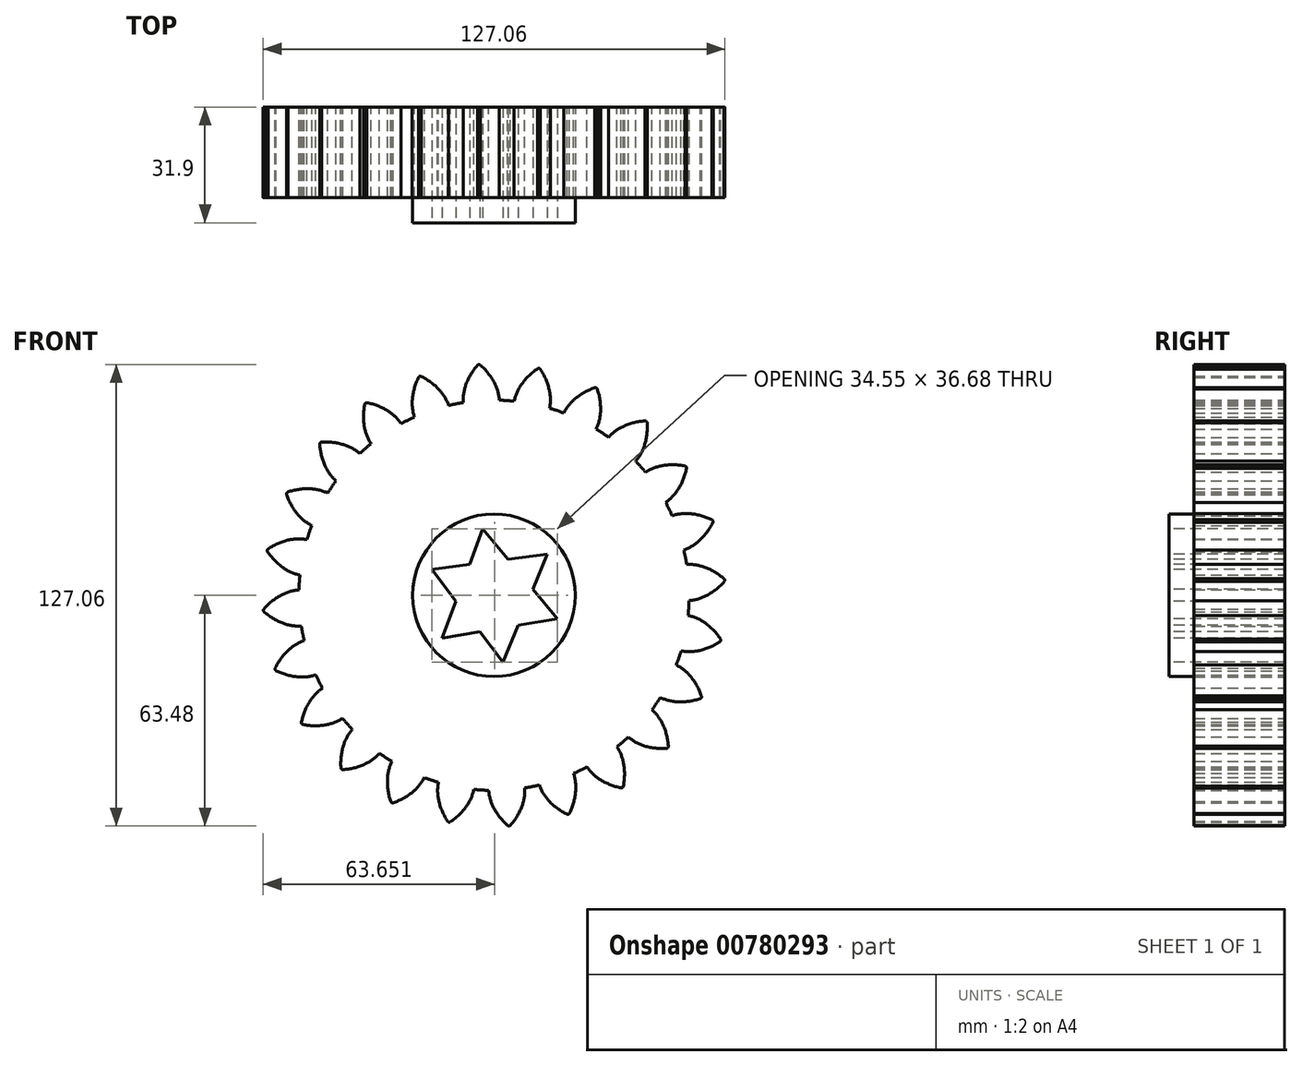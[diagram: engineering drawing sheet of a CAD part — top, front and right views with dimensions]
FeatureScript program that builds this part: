
annotation { "Feature Type Name" : "Feature", "Feature Type Description" : "" }
export const myFeature = defineFeature(function(context is Context, id is Id, definition is map)
    precondition{}
    {
        {
            var Q0;
            Q0=qCreatedBy(makeId("Front.planeOp"),FACE);
            var sketch = newSketch(context, id + "F0", { "sketchPlane" : qUnion([Q0])});
            skCircle(sketch, "E0", {"center": v(0, 0) * mm, "radius": 63.5 * mm, "construction": true});
            skCircle(sketch, "E1", {"center": v(0, 0) * mm, "radius": 53.72 * mm});
            skCircle(sketch, "E2", {"center": v(0, 0) * mm, "radius": 58.67 * mm, "construction": true});
            skLineSegment(sketch, "E3", {"start": v(0, 0) * mm, "end": v(0, 67.7) * mm, "construction": true});
            skLineSegment(sketch, "E4", {"start": v(0, 0) * mm, "end": v(-4.77, 72.78) * mm, "construction": true});
            skLineSegment(sketch, "E5", {"start": v(0, 58.67) * mm, "end": v(-82.08, 58.67) * mm, "construction": true});
            skLineSegment(sketch, "E6", {"start": v(0, 58.67) * mm, "end": v(-77.26, 24.74) * mm, "construction": true});
            skCircle(sketch, "E7", {"center": v(0, 58.67) * mm, "radius": 14.6 * mm, "construction": true});
            skCircle(sketch, "E8", {"center": v(0, 0) * mm, "radius": 53.72 * mm, "construction": true});
            skCircle(sketch, "E9", {"center": v(-13.05, 52.11) * mm, "radius": 14.6 * mm, "construction": true});
            skArc(sketch, "E10", {"start": v(0, 58.67) * mm, "mid": v(-1.67, 61.2) * mm, "end": v(-3.77, 63.39) * mm});
            skArc(sketch, "E11", {"start": v(1.47, 53.7) * mm, "mid": v(1, 56.26) * mm, "end": v(0, 58.67) * mm});
            skArc(sketch, "E12.MirrorCS", {"start": v(-7.66, 58.17) * mm, "mid": v(-6.33, 60.9) * mm, "end": v(-4.54, 63.34) * mm});
            skArc(sketch, "E13", {"start": v(-3.77, 63.39) * mm, "mid": v(-4.16, 63.53) * mm, "end": v(-4.54, 63.34) * mm});
            skArc(sketch, "E14.MirrorCS", {"start": v(-8.47, 53.05) * mm, "mid": v(-8.33, 55.65) * mm, "end": v(-7.66, 58.17) * mm});
            skSolve(sketch);
        }
        {
            var Q0;
            Q0 = qSketchRegion(id + "F0", true);
            extrude(context, id + "F1", {"entities" : qUnion([Q0]), "depth" : 25 * mm, "offsetDistance" : 25 * mm});
        }
        {
            var Q0;
            Q0=makeQuery(id+"F1.opExtrude","SWEPT_BODY",BODY,{"disambiguationData":[OSD([sQuery(id+"F0.wireOp",EDGE,"E1"),sQuery(id+"F0.wireOp",EDGE,"E10"),sQuery(id+"F0.wireOp",EDGE,"E11"),sQuery(id+"F0.wireOp",EDGE,"E12.MirrorCS"),sQuery(id+"F0.wireOp",EDGE,"E13"),sQuery(id+"F0.wireOp",EDGE,"E14.MirrorCS")])]});
            var Q1;
            Q1=makeQuery(id+"F1.opExtrude","SWEPT_FACE",FACE,{"disambiguationData":[OSD([sQuery(id+"F0.wireOp",EDGE,"E1")])]});
            circularPattern(context, id + "F2", {"operationType" : NewBodyOperationType.ADD, "entities" : qUnion([Q0]), "axis" : qUnion([Q1]), "angle" : 360 * degree, "instanceCount" : 24, "equalSpace" : true});
        }
        {
            var Q0;
            {var subQ0=makeQuery(id+"F1.opExtrude","CAP_FACE",FACE,{"disambiguationData":[OSD([sQuery(id+"F0.wireOp",EDGE,"E1"),sQuery(id+"F0.wireOp",EDGE,"E10"),sQuery(id+"F0.wireOp",EDGE,"E11"),sQuery(id+"F0.wireOp",EDGE,"E12.MirrorCS"),sQuery(id+"F0.wireOp",EDGE,"E13"),sQuery(id+"F0.wireOp",EDGE,"E14.MirrorCS")])],"isStart":false});Q0=makeQuery(id+"F2.boolean.opBoolean","MERGE",FACE,{"derivedFrom":[subQ0,makeQuery(id+"F2.opPattern","COPY",FACE,{"derivedFrom":subQ0,"instanceName":"1"}),makeQuery(id+"F2.opPattern","COPY",FACE,{"derivedFrom":subQ0,"instanceName":"2"}),makeQuery(id+"F2.opPattern","COPY",FACE,{"derivedFrom":subQ0,"instanceName":"3"}),makeQuery(id+"F2.opPattern","COPY",FACE,{"derivedFrom":subQ0,"instanceName":"4"}),makeQuery(id+"F2.opPattern","COPY",FACE,{"derivedFrom":subQ0,"instanceName":"5"}),makeQuery(id+"F2.opPattern","COPY",FACE,{"derivedFrom":subQ0,"instanceName":"6"}),makeQuery(id+"F2.opPattern","COPY",FACE,{"derivedFrom":subQ0,"instanceName":"7"}),makeQuery(id+"F2.opPattern","COPY",FACE,{"derivedFrom":subQ0,"instanceName":"8"}),makeQuery(id+"F2.opPattern","COPY",FACE,{"derivedFrom":subQ0,"instanceName":"9"}),makeQuery(id+"F2.opPattern","COPY",FACE,{"derivedFrom":subQ0,"instanceName":"10"}),makeQuery(id+"F2.opPattern","COPY",FACE,{"derivedFrom":subQ0,"instanceName":"11"}),makeQuery(id+"F2.opPattern","COPY",FACE,{"derivedFrom":subQ0,"instanceName":"12"}),makeQuery(id+"F2.opPattern","COPY",FACE,{"derivedFrom":subQ0,"instanceName":"13"}),makeQuery(id+"F2.opPattern","COPY",FACE,{"derivedFrom":subQ0,"instanceName":"14"}),makeQuery(id+"F2.opPattern","COPY",FACE,{"derivedFrom":subQ0,"instanceName":"15"}),makeQuery(id+"F2.opPattern","COPY",FACE,{"derivedFrom":subQ0,"instanceName":"16"}),makeQuery(id+"F2.opPattern","COPY",FACE,{"derivedFrom":subQ0,"instanceName":"17"}),makeQuery(id+"F2.opPattern","COPY",FACE,{"derivedFrom":subQ0,"instanceName":"18"}),makeQuery(id+"F2.opPattern","COPY",FACE,{"derivedFrom":subQ0,"instanceName":"19"}),makeQuery(id+"F2.opPattern","COPY",FACE,{"derivedFrom":subQ0,"instanceName":"20"}),makeQuery(id+"F2.opPattern","COPY",FACE,{"derivedFrom":subQ0,"instanceName":"21"}),makeQuery(id+"F2.opPattern","COPY",FACE,{"derivedFrom":subQ0,"instanceName":"22"}),makeQuery(id+"F2.opPattern","COPY",FACE,{"derivedFrom":subQ0,"instanceName":"23"})]});}
            var sketch = newSketch(context, id + "F3", { "sketchPlane" : qUnion([Q0])});
            skCircle(sketch, "E15", {"center": v(0, 0) * mm, "radius": 22.38 * mm});
            skSolve(sketch);
        }
        {
            var Q0;
            Q0=makeQuery(id+"F3.imprint","IMPRINT",FACE,{"disambiguationData":[TD([[makeQuery(id+"F3.imprint","IMPRINT",EDGE,{"derivedFrom":sQuery(id+"F3.wireOp",EDGE,"E15")}),1.0]])]});
            extrude(context, id + "F4", {"entities" : qUnion([Q0]), "operationType" : NewBodyOperationType.ADD, "depth" : 6.9 * mm, "offsetDistance" : 25 * mm});
        }
        {
            var Q0;
            Q0=makeQuery(id+"F4.opExtrude","CAP_FACE",FACE,{"disambiguationData":[OSD([sQuery(id+"F3.wireOp",EDGE,"E15")])],"isStart":false});
            var sketch = newSketch(context, id + "F5", { "sketchPlane" : qUnion([Q0])});
            skCircle(sketch, "E16.cCircle", {"center": v(0, 0) * mm, "radius": 9.28 * mm, "construction": true});
            skLineSegment(sketch, "E16.0", {"start": v(-17.15, 7.08) * mm, "end": v(14.7, 11.32) * mm});
            skLineSegment(sketch, "E16.1", {"start": v(14.7, 11.32) * mm, "end": v(2.45, -18.4) * mm});
            skLineSegment(sketch, "E16.2", {"start": v(2.45, -18.4) * mm, "end": v(-17.15, 7.08) * mm});
            skPoint(sketch, "E16.0.midPoint", {"position": v(-1.22, 9.2) * mm});
            skLineSegment(sketch, "E17.0", {"start": v(-3.1, 18.3) * mm, "end": v(17.4, -6.46) * mm});
            skLineSegment(sketch, "E17.1", {"start": v(17.4, -6.46) * mm, "end": v(-14.29, -11.84) * mm});
            skLineSegment(sketch, "E17.2", {"start": v(-14.29, -11.84) * mm, "end": v(-3.1, 18.3) * mm});
            skPoint(sketch, "E17.0.midPoint", {"position": v(7.14, 5.92) * mm});
            skSolve(sketch);
        }
        {
            var Q0;
            {var subQ0=sQuery(id+"F5.wireOp",EDGE,"E16.2");var subQ1=sQuery(id+"F5.wireOp",EDGE,"E16.0");var subQ2=makeQuery(id+"F5.imprint","INTERSECT",VERTEX,{"derivedFrom":[subQ1,subQ0]});Q0=makeQuery(id+"F5.imprint","IMPRINT",FACE,{"disambiguationData":[TD([[makeQuery(id+"F5.imprint","IMPRINT",EDGE,{"disambiguationData":[TD([[subQ2,-1.0]])],"derivedFrom":subQ1}),-1.0]])]});}
            var Q1;
            {var subQ0=sQuery(id+"F5.wireOp",EDGE,"E17.2");var subQ1=sQuery(id+"F5.wireOp",EDGE,"E16.0");var subQ2=makeQuery(id+"F5.imprint","INTERSECT",VERTEX,{"derivedFrom":[subQ1,subQ0]});Q1=makeQuery(id+"F5.imprint","IMPRINT",FACE,{"disambiguationData":[TD([[makeQuery(id+"F5.imprint","IMPRINT",EDGE,{"disambiguationData":[TD([[subQ2,-1.0]])],"derivedFrom":subQ1}),1.0]])]});}
            var Q2;
            {var subQ0=sQuery(id+"F5.wireOp",EDGE,"E16.1");var subQ1=sQuery(id+"F5.wireOp",EDGE,"E16.0");var subQ2=makeQuery(id+"F5.imprint","INTERSECT",VERTEX,{"derivedFrom":[subQ1,subQ0]});Q2=makeQuery(id+"F5.imprint","IMPRINT",FACE,{"disambiguationData":[TD([[makeQuery(id+"F5.imprint","IMPRINT",EDGE,{"disambiguationData":[TD([[subQ2,1.0]])],"derivedFrom":subQ1}),-1.0]])]});}
            var Q3;
            {var subQ0=sQuery(id+"F5.wireOp",EDGE,"E17.0");var subQ1=sQuery(id+"F5.wireOp",EDGE,"E16.1");var subQ2=makeQuery(id+"F5.imprint","INTERSECT",VERTEX,{"derivedFrom":[subQ1,subQ0]});Q3=makeQuery(id+"F5.imprint","IMPRINT",FACE,{"disambiguationData":[TD([[makeQuery(id+"F5.imprint","IMPRINT",EDGE,{"disambiguationData":[TD([[subQ2,-1.0]])],"derivedFrom":subQ1}),1.0]])]});}
            var Q4;
            {var subQ0=sQuery(id+"F5.wireOp",EDGE,"E16.2");var subQ1=sQuery(id+"F5.wireOp",EDGE,"E16.1");var subQ2=makeQuery(id+"F5.imprint","INTERSECT",VERTEX,{"derivedFrom":[subQ1,subQ0]});Q4=makeQuery(id+"F5.imprint","IMPRINT",FACE,{"disambiguationData":[TD([[makeQuery(id+"F5.imprint","IMPRINT",EDGE,{"disambiguationData":[TD([[subQ2,1.0]])],"derivedFrom":subQ1}),-1.0]])]});}
            var Q5;
            {var subQ0=sQuery(id+"F5.wireOp",EDGE,"E17.1");var subQ1=sQuery(id+"F5.wireOp",EDGE,"E16.2");var subQ2=makeQuery(id+"F5.imprint","INTERSECT",VERTEX,{"derivedFrom":[subQ1,subQ0]});Q5=makeQuery(id+"F5.imprint","IMPRINT",FACE,{"disambiguationData":[TD([[makeQuery(id+"F5.imprint","IMPRINT",EDGE,{"disambiguationData":[TD([[subQ2,-1.0]])],"derivedFrom":subQ1}),1.0]])]});}
            var Q6;
            {var subQ1=sQuery(id+"F5.wireOp",EDGE,"E16.0");var subQ8=sQuery(id+"F5.wireOp",EDGE,"E17.2");var subQ11=makeQuery(id+"F5.imprint","INTERSECT",VERTEX,{"derivedFrom":[subQ1,subQ8]});Q6=makeQuery(id+"F5.imprint","IMPRINT",FACE,{"disambiguationData":[TD([[makeQuery(id+"F5.imprint","IMPRINT",EDGE,{"disambiguationData":[TD([[subQ11,-1.0]])],"derivedFrom":subQ1}),-1.0]])]});}
            extrude(context, id + "F6", {"entities" : qUnion([Q0, Q1, Q2, Q3, Q4, Q5, Q6]), "operationType" : NewBodyOperationType.REMOVE, "oppositeDirection" : true, "depth" : 250 * mm, "offsetDistance" : 25 * mm});
        }
    });
